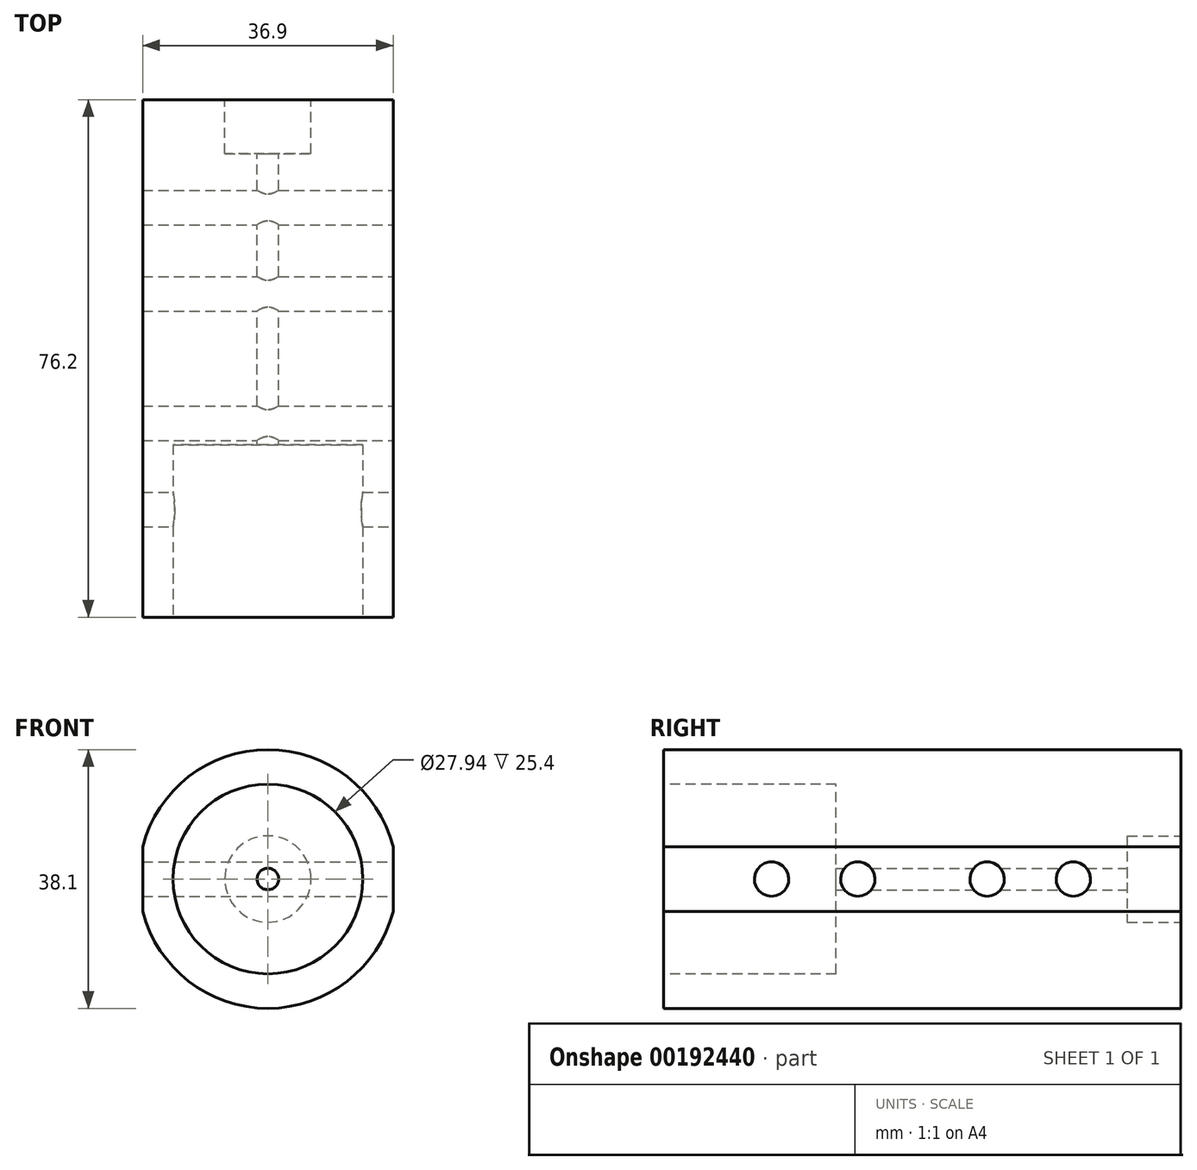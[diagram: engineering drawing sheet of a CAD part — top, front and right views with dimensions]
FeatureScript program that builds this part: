
annotation { "Feature Type Name" : "Feature", "Feature Type Description" : "" }
export const myFeature = defineFeature(function(context is Context, id is Id, definition is map)
    precondition{}
    {
        {
            var Q0;
            Q0=qCreatedBy(makeId("Front.planeOp"),FACE);
            var sketch = newSketch(context, id + "F0", { "sketchPlane" : qUnion([Q0])});
            skCircle(sketch, "E0", {"center": v(0, 0) * mm, "radius": 19.05 * mm});
            skSolve(sketch);
        }
        {
            var Q0;
            Q0 = qSketchRegion(id + "F0", true);
            extrude(context, id + "F1", {"entities" : qUnion([Q0]), "depth" : 76.2 * mm});
        }
        {
            var Q0;
            Q0=makeQuery(id+"F1.opExtrude","CAP_FACE",FACE,{"disambiguationData":[OSD([sQuery(id+"F0.wireOp",EDGE,"E0")])],"isStart":false});
            var sketch = newSketch(context, id + "F2", { "sketchPlane" : qUnion([Q0])});
            skCircle(sketch, "E1", {"center": v(0, 0) * mm, "radius": 13.97 * mm});
            skSolve(sketch);
        }
        {
            var Q0;
            Q0 = qSketchRegion(id + "F2", true);
            extrude(context, id + "F3", {"entities" : qUnion([Q0]), "operationType" : NewBodyOperationType.REMOVE, "oppositeDirection" : true, "depth" : 25.4 * mm});
        }
        {
            var Q0;
            Q0=makeQuery(id+"F1.opExtrude","CAP_FACE",FACE,{"disambiguationData":[OSD([sQuery(id+"F0.wireOp",EDGE,"E0")])],"isStart":false});
            var sketch = newSketch(context, id + "F4", { "sketchPlane" : qUnion([Q0])});
            skLineSegment(sketch, "E2.left", {"start": v(18.45, 4.76) * mm, "end": v(18.45, -4.76) * mm});
            skLineSegment(sketch, "E2.right", {"start": v(-18.45, 4.76) * mm, "end": v(-18.45, -4.76) * mm});
            skPoint(sketch, "E2.middle", {"position": v(0, 0) * mm});
            skArc(sketch, "E3", {"start": v(-18.45, 4.76) * mm, "mid": v(-19.05, 0) * mm, "end": v(-18.45, -4.76) * mm});
            skArc(sketch, "E4.trimOffspring", {"start": v(18.45, -4.76) * mm, "mid": v(19.05, 0) * mm, "end": v(18.45, 4.76) * mm});
            skSolve(sketch);
        }
        {
            var Q0;
            Q0 = qSketchRegion(id + "F4", true);
            extrude(context, id + "F5", {"entities" : qUnion([Q0]), "operationType" : NewBodyOperationType.REMOVE, "endBound" : BoundingType.THROUGH_ALL, "oppositeDirection" : true, "depth" : 25.4 * mm});
        }
        {
            var Q0;
            Q0=makeQuery(id+"F5.boolean.opBoolean","COPY",FACE,{"derivedFrom":makeQuery(id+"F5.opExtrude","SWEPT_FACE",FACE,{"disambiguationData":[OSD([sQuery(id+"F4.wireOp",EDGE,"E2.left")])]})});
            var sketch = newSketch(context, id + "F6", { "sketchPlane" : qUnion([Q0])});
            skCircle(sketch, "E5", {"center": v(-60.33, 0) * mm, "radius": 2.54 * mm});
            skPoint(sketch, "E5.centerSnap0", {"position": v(-76.2, 0) * mm});
            skCircle(sketch, "E6", {"center": v(-47.62, 0) * mm, "radius": 2.54 * mm});
            skCircle(sketch, "E7", {"center": v(-28.58, 0) * mm, "radius": 2.54 * mm});
            skCircle(sketch, "E8", {"center": v(-15.88, 0) * mm, "radius": 2.54 * mm});
            skSolve(sketch);
        }
        {
            var Q0;
            Q0 = qSketchRegion(id + "F6", true);
            extrude(context, id + "F7", {"entities" : qUnion([Q0]), "operationType" : NewBodyOperationType.REMOVE, "endBound" : BoundingType.THROUGH_ALL, "oppositeDirection" : true, "depth" : 25.4 * mm});
        }
        {
            var Q0;
            Q0=makeQuery(id+"F1.opExtrude","CAP_FACE",FACE,{"disambiguationData":[OSD([sQuery(id+"F0.wireOp",EDGE,"E0")])],"isStart":true});
            var sketch = newSketch(context, id + "F8", { "sketchPlane" : qUnion([Q0])});
            skCircle(sketch, "E9", {"center": v(0, 0) * mm, "radius": 6.35 * mm});
            skSolve(sketch);
        }
        {
            var Q0;
            Q0 = qSketchRegion(id + "F8", true);
            extrude(context, id + "F9", {"entities" : qUnion([Q0]), "operationType" : NewBodyOperationType.REMOVE, "oppositeDirection" : true, "depth" : 7.94 * mm});
        }
        {
            var Q0;
            Q0=makeQuery(id+"F9.boolean.opBoolean","COPY",FACE,{"derivedFrom":makeQuery(id+"F9.opExtrude","CAP_FACE",FACE,{"disambiguationData":[OSD([sQuery(id+"F8.wireOp",EDGE,"E9")])],"isStart":false})});
            var sketch = newSketch(context, id + "F10", { "sketchPlane" : qUnion([Q0])});
            skCircle(sketch, "E10", {"center": v(0, 0) * mm, "radius": 1.59 * mm});
            skSolve(sketch);
        }
        {
            var Q0;
            Q0 = qSketchRegion(id + "F10", true);
            extrude(context, id + "F11", {"entities" : qUnion([Q0]), "operationType" : NewBodyOperationType.REMOVE, "endBound" : BoundingType.THROUGH_ALL, "oppositeDirection" : true, "depth" : 25.4 * mm});
        }
    });
